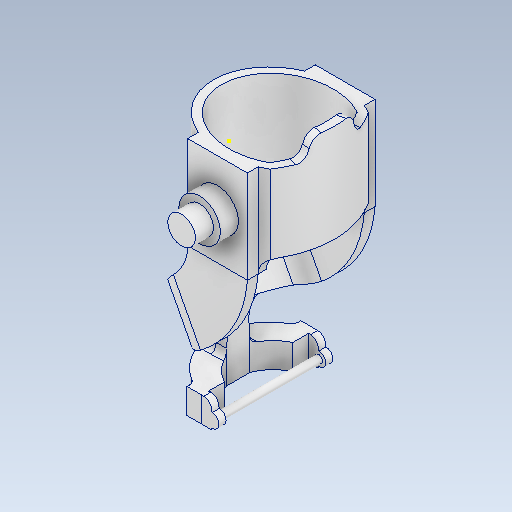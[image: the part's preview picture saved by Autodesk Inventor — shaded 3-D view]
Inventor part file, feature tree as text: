
AUTODESK INVENTOR PART (.ipt)
format: ipt  version: 2021 (Build 250183000, 183)  size: 1,129,472 bytes
history: native  units: mm
features: sketch x30, plane x7, other x3
ambient origin geometry x8: Origin, YZ Plane, XZ Plane, XY Plane, X Axis, Y Axis, Z Axis, Center Point
bodies: Solid1 (feature_tree)
feature tree (40):
  other  "CRUS FRAME.ipt"
  other  "Solid1::CRUS FRAME.ipt"
  other  "TaggingFeature1"
  sketch  "Sketch1"  dims[d0=10.0mm]
  sketch  "Sketch2"
  sketch  "Sketch5"
  sketch  "Sketch6"
  sketch  "Sketch7"
  sketch  "Sketch8"
  sketch  "Sketch9"
  sketch  "Sketch12"
  sketch  "Sketch13"
  sketch  "Sketch14"
  sketch  "Sketch16"
  sketch  "Sketch17"
  sketch  "Sketch18"
  sketch  "Sketch19"
  sketch  "Sketch20"
  sketch  "Sketch23"
  sketch  "Sketch25"
  sketch  "Sketch27"
  sketch  "Sketch29"
  sketch  "Sketch30"
  sketch  "Sketch32"
  sketch  "Sketch33"
  sketch  "Sketch34"
  sketch  "Sketch37"
  sketch  "Sketch38"
  sketch  "Sketch39"
  sketch  "Sketch40"
  sketch  "Sketch41"
  sketch  "Sketch42"
  sketch  "Sketch43"
  plane  "Work Plane1"
  plane  "Work Plane2"
  plane  "Work Plane3"
  plane  "Work Plane4"
  plane  "Work Plane5"
  plane  "Work Plane6"
  plane  "Work Plane11"
